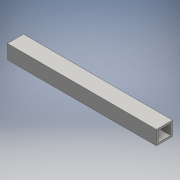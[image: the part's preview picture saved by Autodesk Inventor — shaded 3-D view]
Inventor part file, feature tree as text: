
AUTODESK INVENTOR PART (.ipt)
format: ipt  version: 2016 (Build 200138000, 138)  size: 99,328 bytes
history: native  units: mm
features: extrude x2, sketch x2
ambient origin geometry x8: Origin, YZ Plane, XZ Plane, XY Plane, X Axis, Y Axis, Z Axis, Center Point
bodies: Body1 (feature_tree)
feature tree (4):
  extrude  "Extrusion2"  Depth=15.0mm
  extrude  "Extrusion3"  Depth=11.0mm
  sketch  "Sketch2"  dims[d4=17.0mm d5=15.0mm]
  sketch  "Sketch3"  dims[d6=157.0mm d7=0.0mm d9=11.0mm d10=13.0mm d11=0.0mm d12=0.0mm]
